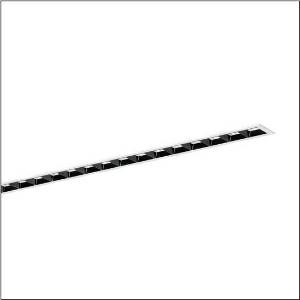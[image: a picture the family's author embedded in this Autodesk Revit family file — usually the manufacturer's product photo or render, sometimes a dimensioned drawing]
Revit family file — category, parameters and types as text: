
# Revit family: silica_r__21_51mx12da44wb_905f
name_source: partatom
category: Lighting Fixtures
units: mm (PartAtom-declared; Revit-internal decimal feet)

## family parameters
Cut with Voids When Loaded = No
Host = Face
Light Source = No
Part Type = Normal
Room Calculation Point = No
Round Connector Dimension = Use Diameter
Shared = No

## types (1)
- --- (1 x LED, 4320 lm, 25.6 W, 4000K)
    Apparent Load = 26 VA
    CIE Flux Codes = 86 100 100 100 100
    Color Rendering = 80
    Color Temperature = 4000K
    Default Elevation = 1800 mm
    Description = Silica® 21, office luminaire, primary light control with darklight reflector, of PMMA, black, CAT 2 (L<= 3000cd/m²), light emission: direct distribution, primary light characteristic: symmetric, installation type: recessed, LED, rated luminous flux: 4.320lm, luminous efficacy: 169lm/W, light colour: 840, colour temperature: 4000K, control gear: DALI 2, with terminal, 3+2-pole, max. 2.5mm², mains connection: 220..240V, AC, 50/60Hz, rated input power: 25.6W, luminaire housing, of aluminium, traffic white (RAL 9016), length: 1.228mm, width: 79mm, height: 53mm, protection rating (complete): IP20, insulation class (complete): insulation class I (protective earthing), certification: CE, ENEC, VDE, permissible operating ambient temperature: 0..+35°C, standard: EN 50419, packaging unit: 1 piece
    Height = 0 mm  [stored 0 ft]
    Lamp = 1 x LED
    Lamp Light Flux = 4320 lm
    Lamp Power = 25.6 W
    Lamp count = 1
    Length = 1227 mm
    Luminous efficacy = 169 lm/W
    Manufacturer = Siteco
    ModVariant = No
    Model = 51MX12DA44WB
    Mounting Place = Ceiling
    Mounting Type = Recessed
    Number of Poles = 1
    OnlyDefault = Yes
    Power Factor = 1
    Product Name = Silica® 21
    Product group = office luminaire | ceiling recessed
    ProductGroupID = 401
    Protection Class = Protection class I
    Protection Degree = IP 20
    RLX_Detail_Level = 1
    RLX_Emergency_Light_Flux = 0 lm
    RLX_Emergency_Type = 0
    RLX_Emergency_Type_DB = No
    RlxData = <blob elided: 39157 chars, md5=d24ba31f>
    Socket = socket
    Standby Power = 0 W
    System Light Flux = 4320 lm
    System Power = 26 W
    Type Comments = factory setting: luminous flux: 100 % | dim-lin: 254 | 367 mA
    Type Image = l_1335880.jpg
    URL = http://relux.com
    VarID = @adj_008625
    Voltage = 0 V
    Weight = 0.00 kg
    Width = 79 mm

note: [stored X ft] marks values corroborated as IEEE doubles in the binary element streams (Revit-internal decimal feet)

## geometry (parser evidence)
native form markers: Blend x4, Sweep x10
no freeform markers — native parametric forms only
